# Revit family: 13-HC_RAS_HCL_TOSHIBA_TCTC_4MU2VAG_27
name_source: partatom
category: Mechanical Equipment
revit_build: Autodesk Revit 2017 (Build: 20160225_1515(x64)
units: mm (PartAtom-declared; Revit-internal decimal feet)

## family parameters
Always vertical = Yes
Cut with Voids When Loaded = No
OmniClass Number = 23.75.00.00
OmniClass Title = Climate Control (HVAC)
Part Type = Normal
Room Calculation Point = No
Round Connector Dimension = Use Diameter
Shared = No
Work Plane-Based = No

## types (1)
- RAS-4M27U2AVG-E
    Airflow m3/h - Cooling/Heating = 2507 / 2507
    Article Description = Multi R32
    Article Type = RAS-4M27U2AVG-E
    Compressor detail - Motor output  (kW) = 2000
    Compressor detail - Type = Hermetic DC twin rotary compressor
    Content Supplier URL = www.hcltech.com
    Custom = No
    Depth (mm) = 320 mm  [stored 1.04987 ft]
    Description = Multi R32
    EMCS = 4
    ETIM Article Class = EC001213
    Energy class-Cooling/Heating = A++ / A++
    Frequency (Hz) = 50Hz
    Height (mm) = 890 mm  [stored 2.91995 ft]
    Hydronic Return Diameter (mm) = 13 mm
    Hydronic Supply Diameter (mm) = 10 mm  [stored 0.0328084 ft]
    MEPcontent Class = HEATPUMP
    MOCP (A) = 20
    Manufacturer = Toshiba
    Manufacturer Art. No. = RAS-4M27U2AVG-E
    Manufacturer URL = https://www.toshiba-carrier.co.jp
    Maximum current A = 10.94
    Model = RAS-4M27U2AVG-E
    Operating range - Cooling (°C) = -10 to 46 degC
    Operating range - Heating (°C) = -15 to 24 degC
    Pdesigh - Cooling/Heating = 8.0 / 5.2
    Power consumption-Cooling (Kw) = 2290
    Power consumption-Heating (Kw) = 1930
    Product Line = TCTC
    Rated Capacity kW- Cooling/Heating = 8.0 / 9.0
    Rated Power Consumption kW - Cooling/Heating = 2290 / 1930
    Rated efficiency EER / COP = 3.50 / 4.67
    Red = Colour RGB-250 000 000
    Refrigerant information = R32
    Running current-Cooling (A) = 10.94/10.46/10.03
    Running current-Heating (A) = 9.22/8.82/8.45
    Seasonal Efficiency-SEER  / SCOP = 6.11 / 4.26
    Sound pressure - Cooling/Heating (dB) = 48 / 49
    URL = https://www.toshiba-carrier.co.jp
    Voltage (V) = 220V-240V
    Weight (Kg) = 72
    White = Colour RGB-255 255 255
    Width (mm) = 900 mm  [stored 2.95276 ft]

note: [stored X ft] marks values corroborated as IEEE doubles in the binary element streams (Revit-internal decimal feet)

## geometry (parser evidence)
native form markers: Sweep x4
no freeform markers — native parametric forms only
